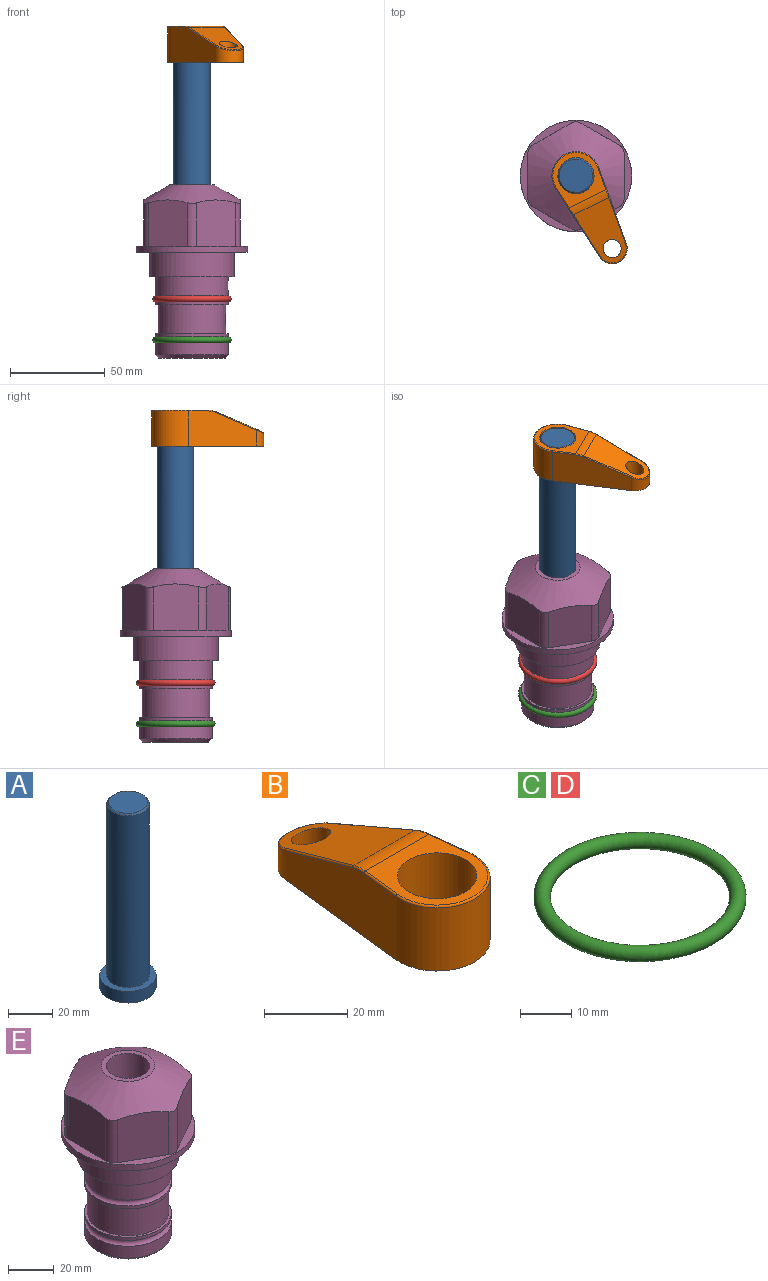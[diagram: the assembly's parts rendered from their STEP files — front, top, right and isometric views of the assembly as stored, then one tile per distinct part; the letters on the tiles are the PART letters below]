
ASSEMBLY  parts=5 mates=3
PART A: 6 faces, bbox 25.4x25.4x101.6 mm
  f0: plane 17.46x17.46mm, normal (0,0,1), area 239.5mm2, adj f5
  f1: plane 25.4x25.4mm, normal (0,0,-1), area 506.7mm2, adj f2
  f2: cylinder r=12.7mm len=25.4mm, axis (0,0,1), area 506.7mm2, adj f1,f3
  f3: plane 25.4x25.4mm, normal (0,0,1), area 221.7mm2, adj f2,f4
  f4: cylinder r=9.53mm len=94.46mm, axis (0,0,1), area 5653mm2, adj f3,f5
  f5: cone r=8.73mm half-angle=45deg, axis (0,0,-1), area 64.4mm2, adj f0,f4
PART B: 44 faces, bbox 27.5x64.5x19.1 mm
  f0: plane 2.3x0.95mm, normal (0,0,-1), area 1mm2, adj f25,f30,f34
  f1: plane 63.5x25.4mm, normal (0,0,-1), area 561.7mm2, adj f2,f3,f4,f5,f6,f7,f19,f20
  f2: cylinder r=12.7mm len=25.4mm, axis (0,0,-1), area 792.2mm2, adj f1,f3,f5,f13
  f3: plane 42.33x18.54mm, normal (0.99,0.11,0), area 647mm2, adj f1,f2,f4,f11,f12,f14
  f4: cylinder r=7.94mm len=15.78mm, axis (0,0,-1), area 158.6mm2, adj f1,f3,f5,f16
  f5: plane 42.33x18.54mm, normal (-0.99,0.11,0), area 647mm2, adj f1,f2,f4,f15,f17,f18
  f6: cylinder r=9.53mm len=19.05mm, axis (0,0,-1), area 1140.1mm2, adj f1,f8
  f7: cylinder r=4.76mm len=10.98mm, axis (0,0,-1), area 276.1mm2, adj f1,f9
  f8: plane 25.83x24.38mm, normal (0,0,1), area 262.2mm2, adj f6,f10,f11,f13,f15
  f9: plane 32.49x20.55mm, normal (0,0.34,0.94), area 489.9mm2, adj f7,f10,f14,f16,f18
  f10: cylinder r=12.7mm len=21.49mm, axis (-1,0,0), area 93.2mm2, adj f8,f9,f12,f17
  f11: cylinder r=0.51mm len=12.34mm, axis (0.11,-0.99,0), area 9.9mm2, adj f3,f8,f12,f13
  f12: bspline ~7.62x1.64mm, area 3.5mm2, adj f3,f10,f11,f14
  f13: torus R=12.19mm, axis (0,0,1), area 33.6mm2, adj f2,f8,f11,f15
  f14: cylinder r=0.51mm len=26.01mm, axis (0.1,-0.93,0.34), area 21.6mm2, adj f3,f9,f12,f16
  f15: cylinder r=0.51mm len=12.34mm, axis (0.11,0.99,0), area 9.9mm2, adj f5,f8,f13,f17
  f16: bspline ~15.78x7.05mm, area 15.7mm2, adj f4,f9,f14,f18
  f17: bspline ~7.62x1.64mm, area 3.5mm2, adj f5,f10,f15,f18
  f18: cylinder r=0.51mm len=26.01mm, axis (0.1,0.93,-0.34), area 21.6mm2, adj f5,f9,f16,f17
  f19: plane 21.6x14.29mm, normal (-0.99,-0.11,0), area 242.6mm2, adj f1,f26,f28,f34,f36,f38
  f20: plane 21.6x14.29mm, normal (0.99,-0.11,0), area 242.6mm2, adj f1,f27,f29,f37,f39,f41
  f21: cylinder r=12.7mm len=14.29mm, axis (0,0,-1), area 173.2mm2, adj f1,f26,f27,f30,f31,f33
  f22: cylinder r=7.94mm len=7.63mm, axis (0,0,-1), area 53.8mm2, adj f1,f28,f29,f42
  f23: plane 2.3x0.95mm, normal (0,0,-1), area 1mm2, adj f25,f33,f37
  f24: plane 17.94x12.32mm, normal (0,-0.34,-0.94), area 191.2mm2, adj f25,f38,f41,f42
  f25: cylinder r=9.53mm len=12.93mm, axis (-1,0,0), area 37.5mm2, adj f0,f23,f24,f31,f36,f39
  f26: cylinder r=1.59mm len=14.29mm, axis (0,0,-1), area 49mm2, adj f1,f19,f21,f32
  f27: cylinder r=1.59mm len=14.29mm, axis (0,0,-1), area 49mm2, adj f1,f20,f21,f35
  f28: cylinder r=1.59mm len=7.28mm, axis (0,0,-1), area 22.1mm2, adj f1,f19,f22,f40
  f29: cylinder r=1.59mm len=7.28mm, axis (0,0,-1), area 22.1mm2, adj f1,f20,f22,f43
  f30: torus R=14.29mm, axis (0,0,1), area 5.8mm2, adj f0,f21,f31,f32
  f31: bspline ~11.06x2.73mm, area 20.8mm2, adj f21,f25,f30,f33
  f32: sphere r=1.59mm, area 5.4mm2, adj f26,f30,f34
  f33: torus R=14.29mm, axis (0,0,1), area 5.8mm2, adj f21,f23,f31,f35
  f34: cylinder r=1.59mm len=1.68mm, axis (-0.11,0.99,0), area 2.4mm2, adj f0,f19,f32,f36
  f35: sphere r=1.59mm, area 5.4mm2, adj f27,f33,f37
  f36: bspline ~5.82x2.33mm, area 7.7mm2, adj f19,f25,f34,f38
  f37: cylinder r=1.59mm len=1.68mm, axis (0.11,0.99,0), area 2.4mm2, adj f20,f23,f35,f39
  f38: cylinder r=1.59mm len=18.33mm, axis (0.1,-0.93,0.34), area 46.7mm2, adj f19,f24,f36,f40
  f39: bspline ~5.82x2.33mm, area 7.7mm2, adj f20,f25,f37,f41
  f40: sphere r=1.59mm, area 3.6mm2, adj f28,f38,f42
  f41: cylinder r=1.59mm len=18.33mm, axis (0.1,0.93,-0.34), area 46.7mm2, adj f20,f24,f39,f43
  f42: bspline ~8.31x1.84mm, area 15.3mm2, adj f22,f24,f40,f43
  f43: sphere r=1.59mm, area 3.6mm2, adj f29,f41,f42
PART C: 1 faces, bbox 44.7x44.7x3.2 mm
  f0: torus R=19.05mm, axis (0,0,1), area 1193.9mm2
PART D: same geometry as C
PART E: 36 faces, bbox 58.7x58.7x91.2 mm
  f0: cylinder r=17.78mm len=35.56mm, axis (0,0,1), area 1670.8mm2, adj f23,f24,f31
  f1: cylinder r=19.05mm len=38.1mm, axis (0,0,1), area 1191.9mm2, adj f26,f27,f30
  f2: plane 58.66x58.66mm, normal (0,0,-1), area 1150.6mm2, adj f3,f28
  f3: cylinder r=29.33mm len=58.66mm, axis (0,0,-1), area 585.1mm2, adj f2,f4
  f4: plane 58.66x58.66mm, normal (0,0,1), area 475.9mm2, adj f3,f5,f6,f7,f8,f9,f10,f11
  f5: plane 24.5x20.32mm, normal (-0.5,0.87,0), area 562.8mm2, adj f4,f15,f16,f17
  f6: plane 24.5x20.32mm, normal (0.5,0.87,0), area 562.8mm2, adj f4,f14,f15,f17
  f7: plane 24.5x23.48mm, normal (1,0,0), area 562.8mm2, adj f4,f13,f14,f17
  f8: plane 24.5x20.32mm, normal (0.5,-0.87,0), area 562.8mm2, adj f4,f12,f13,f17
  f9: plane 24.5x20.32mm, normal (-0.5,-0.87,0), area 562.8mm2, adj f4,f11,f12,f17
  f10: plane 24.5x23.48mm, normal (-1,0,0), area 562.8mm2, adj f4,f11,f16,f17
  f11: cylinder r=5.08mm len=23.01mm, axis (0,0,-1), area 121.2mm2, adj f4,f9,f10,f17
  f12: cylinder r=5.08mm len=23.01mm, axis (0,0,-1), area 121.2mm2, adj f4,f8,f9,f17
  f13: cylinder r=5.08mm len=23.01mm, axis (0,0,-1), area 121.2mm2, adj f4,f7,f8,f17
  f14: cylinder r=5.08mm len=23.01mm, axis (0,0,-1), area 121.2mm2, adj f4,f6,f7,f17
  f15: cylinder r=5.08mm len=23.01mm, axis (0,0,-1), area 121.2mm2, adj f4,f5,f6,f17
  f16: cylinder r=5.08mm len=23.01mm, axis (0,0,-1), area 121.2mm2, adj f4,f5,f10,f17
  f17: cone r=11.73mm half-angle=60deg, axis (0,0,-1), area 2071.8mm2, adj f5,f6,f7,f8,f9,f10,f11,f12
  f18: plane 23.46x23.46mm, normal (0,0,1), area 147.4mm2, adj f17,f35
  f19: plane 34.93x34.93mm, normal (0,0,-1), area 958mm2, adj f29
  f20: cylinder r=19.05mm len=38.1mm, axis (0,0,1), area 760.1mm2, adj f21,f29
  f21: torus R=19.05mm, axis (0,0,1), area 565.3mm2, adj f20,f22
  f22: cylinder r=19.05mm len=38.1mm, axis (0,0,1), area 190mm2, adj f21,f23
  f23: plane 38.1x38.1mm, normal (0,0,1), area 146.9mm2, adj f0,f22
  f24: plane 38.1x38.1mm, normal (0,0,-1), area 146.9mm2, adj f0,f25
  f25: cylinder r=19.05mm len=38.1mm, axis (0,0,1), area 190mm2, adj f24,f26
  f26: torus R=19.05mm, axis (0,0,1), area 565.3mm2, adj f1,f25
  f27: plane 44.45x44.45mm, normal (0,0,-1), area 411.7mm2, adj f1,f28
  f28: cylinder r=22.23mm len=44.45mm, axis (0,0,1), area 1773.5mm2, adj f2,f27
  f29: cone r=19.05mm half-angle=45deg, axis (0,0,1), area 257.5mm2, adj f19,f20
  f30: cylinder r=3.17mm len=6.75mm, axis (-1,0,0), area 128mm2, adj f1,f33
  f31: cylinder r=3.17mm len=6.35mm, axis (-1,0,0), area 102.5mm2, adj f0,f33
  f32: plane 25.4x25.4mm, normal (0,0,1), area 506.7mm2, adj f33
  f33: cylinder r=12.7mm len=66.42mm, axis (0,0,-1), area 5236.2mm2, adj f30,f31,f32,f34
  f34: cone r=9.53mm half-angle=30deg, axis (0,0,-1), area 443.4mm2, adj f33,f35
  f35: cylinder r=9.53mm len=19.05mm, axis (0,0,-1), area 849mm2, adj f18,f34
PLACE A rot(axis=(0,0,-1),63.6deg) t=(0,0,45.65)mm
PLACE B rot(axis=(0,0,-1),153.6deg) t=(0,0,100.26)mm
PLACE C t=(0,0,-21.59)mm
PLACE D at identity
PLACE E at identity fixed
MATE fastened C.f0 <-> E.f0  axis (0,0,1) through (0,0,-46.1)mm
MATE cylindrical A.f2 <-> E.f0  axis (0,0,1) through (0,0,71.28)mm
MATE fastened B.f2 <-> A.f2  axis (0,0,1) through (0,0,119.31)mm
